# Revit family: Холодильные столы для приготовления пиццы_1
name_source: partatom
category: Оборудование
units: mm (PartAtom-declared; Revit-internal decimal feet)

## family parameters
Всегда вертикально = Да
Классификация = Нет
На основе рабочей плоскости = Нет
Общий = Нет
При загрузке вырезать с полостями = Нет
Размер круглого соединителя = Использовать диаметр
Тип детали = Нормальный
Точка расчета площади = Нет

## types (14) — shared parameters
Высота = 850 мм
Дверь G-3 = Нет
Диап. рабочих темп. = -2....+10
Напряжение питания = 230.00 В
Степень защиты = IP24
Терморегулятор = эл. блок
Тип оттайки = авт. с системой исп. конденсата
Тип охлаждения = динамический
Условия окр. среды (темп/влажн) = до +43
Хладаген = R134a
Холодильный стол = нержавеющая сталь
zero-valued in all types: Отметка по умолчанию

## per-type parameters (varying)
| type | Боковая панель упр. | Боковая панель упр. (3 решетки) | Вес нетто/брутто, кг | Габаритные размеры, мм | Глубина | Дверь G - 1 | Дверь G-2 | Дверь G-4 | Количество дверей | Нижнее распол Дверь -1 | Нижнее распол. Дверь -2 | Нижняя панель упр. | Объем, л | Размеры в упоковке, мм | Таблица поиска | Цена, руб | Ширина |
| TMi4pizza-G | Нет | Нет | - | 1850х600х850/1000 | 600 мм | Нет | Нет | Нет | 4 | Да | Да | Да | 306 | 2000х714х1140 | ТM | 137 000 | 1850 мм |
| TMi2pizza-G | Нет | Нет | - | 900х600х850/1000 | 600 мм | Нет | Нет | Нет | 2 | Да | Нет | Да | 153 | 1045х714х1040 | ТM | 85 700 | 900 мм |
| TMi3pizza-G | Нет | Нет | - | 1375х600х850/1000 | 600 мм | Нет | Нет | Нет | 3 | Да | Нет | Да | 230 | 1520х714х1140 | ТМ | 109 600 | 1375 мм |
| TM2pizza-G | Нет | Да | 160/200 | 1200х605х850/1000 | 605 мм | Да | Да | Нет | 2 | Нет | Нет | Нет | 270 | 1310х815х1070 | ТM | 96 994 | 1200 мм |
| TM3GNpizza-G | Нет | Да | 200/240 | 1630х705х850/1000 | 705 мм | Да | Да | Да | 3 | Нет | Нет | Нет | 450 | 1725х815х1070 | ТM | 115 858 | 1630 мм |
| TM2pizza-GC | Да | Нет | 160/200 | 1200х605х850/1000 | 605 мм | Да | Да | Нет | 2 | Нет | Нет | Нет | 270 | 1310х815х1070 | ТB | 94 957 | 1200 мм |
| TM3GNpizza-GC | Да | Нет | 200/240 | 1630х705х850/1000 | 705 мм | Да | Да | Да | 3 | Нет | Нет | Нет | 450 | 1725х815х1070 | ТM | 112 137 | 1630 мм |
| TM2GNpizza-G | Нет | Да | 170/210 | 1200х705х850/1000 | 705 мм | Да | Да | Нет | 2 | Нет | Нет | Нет | 320 | 1310х815х1070 | ТM | 104 136 | 1200 мм |
| TM3pizza-G | Нет | Да | 200/240 | 1630х605х850/1000 | 605 мм | Да | Да | Да | 3 | Нет | Нет | Нет | 400 | 1725х815х1070 | ТM | 112 793 | 1630 мм |
| TM2GNpizza-GC | Да | Нет | 170/210 | 1200х705х850/1000 | 705 мм | Да | Да | Нет | 2 | Нет | Нет | Нет | 320 | 1310х815х1070 | ТM | 101 689 | 1200 мм |
| TM3pizza-GC | Да | Нет | 190/230 | 1630х605х850/1000 | 705 мм | Да | Да | Да | 3 | Нет | Нет | Нет | 400 | 1725х815х1070 | ТM | 109 851 | 1630 мм |
| TMi2GNpizza-G | Нет | Нет | - | 900х700х850/1000 | 700 мм | Нет | Нет | Нет | 2 | Да | Нет | Да | 184 | 1045х814х1040 | ТM | 90 265 | 900 мм |
| TMi3GNpizza-G | Нет | Нет | - | 1375х600х850/1000 | 700 мм | Нет | Нет | Нет | 3 | Да | Нет | Да | 276 | 1520х814х1140 | ТМ | 113 500 | 1375 мм |
| TMi4GNpizza-G | Нет | Нет | - | 1850х700х850/1000 | 700 мм | Нет | Нет | Нет | 4 | Да | Да | Да | 368 | 2000х814х1140 | ТM | 139 990 | 1850 мм |
